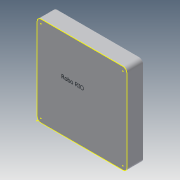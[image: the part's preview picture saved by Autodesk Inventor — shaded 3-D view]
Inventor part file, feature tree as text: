
AUTODESK INVENTOR PART (.ipt)
format: ipt  version: 2014 (Build 180170000, 170)  size: 84,480 bytes
history: native  units: in
note: dims shown in document units (in); Inventor stores cm internally (conversion verified against a paired STEP export)
features: sketch x2, extrude x1
ambient origin geometry x8: Origin, YZ Plane, XZ Plane, XY Plane, X Axis, Y Axis, Z Axis, Center Point
bodies: Solid1 (feature_tree)
feature tree (3):
  extrude  "Extrusion1"  Depth=5.625in
  sketch  "Sketch2"  dims[d2=0.25in d3=1.0in d4=0.0in]
  sketch  "Sketch1"  dims[d0=5.625in d1=5.625in]
